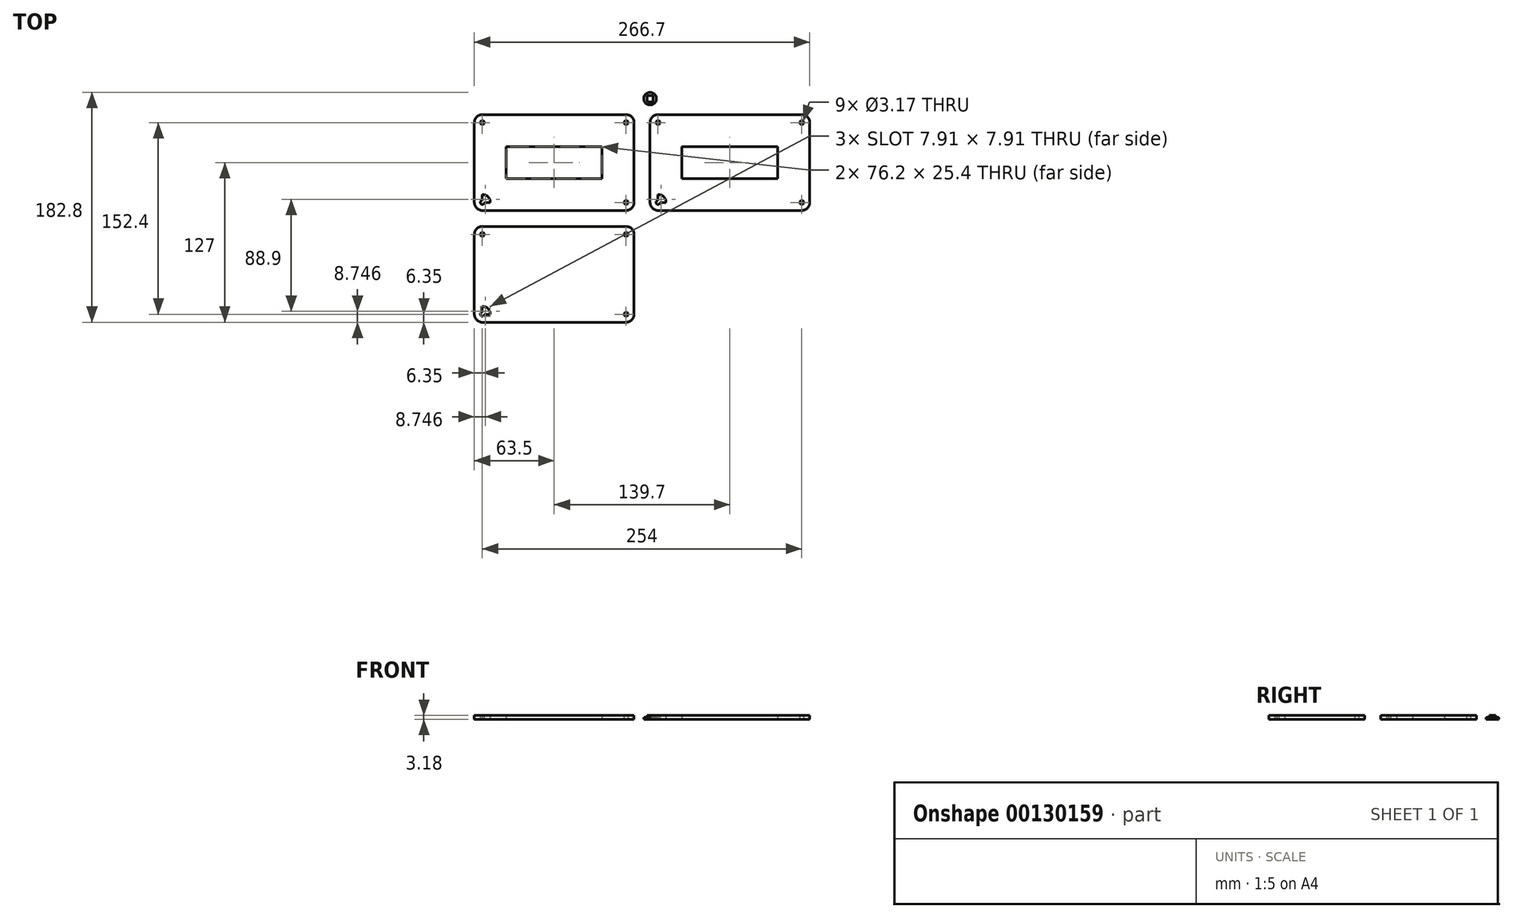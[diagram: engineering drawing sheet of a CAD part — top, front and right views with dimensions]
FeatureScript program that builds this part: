
annotation { "Feature Type Name" : "Feature", "Feature Type Description" : "" }
export const myFeature = defineFeature(function(context is Context, id is Id, definition is map)
    precondition{}
    {
        {
            var Q0;
            Q0=qCreatedBy(makeId("Top.planeOp"),FACE);
            var sketch = newSketch(context, id + "F0", { "sketchPlane" : qUnion([Q0])});
            skCircle(sketch, "E0", {"center": v(0, 0) * mm, "radius": 5 * mm});
            skLineSegment(sketch, "E1.bottom", {"start": v(-2.5, 2.5) * mm, "end": v(2.5, 2.5) * mm});
            skLineSegment(sketch, "E1.top", {"start": v(-2.5, -2.5) * mm, "end": v(2.5, -2.5) * mm});
            skLineSegment(sketch, "E1.left", {"start": v(-2.5, 2.5) * mm, "end": v(-2.5, -2.5) * mm});
            skLineSegment(sketch, "E1.right", {"start": v(2.5, 2.5) * mm, "end": v(2.5, -2.5) * mm});
            skLineSegment(sketch, "E2.bottom", {"start": v(6.35, -12.7) * mm, "end": v(120.65, -12.7) * mm});
            skLineSegment(sketch, "E2.top", {"start": v(6.35, -88.9) * mm, "end": v(120.65, -88.9) * mm});
            skLineSegment(sketch, "E2.left", {"start": v(0, -19.05) * mm, "end": v(0, -82.55) * mm});
            skLineSegment(sketch, "E2.right", {"start": v(127, -19.05) * mm, "end": v(127, -82.55) * mm});
            skLineSegment(sketch, "E3.bottom", {"start": v(25.4, -38.1) * mm, "end": v(101.6, -38.1) * mm});
            skLineSegment(sketch, "E3.top", {"start": v(25.4, -63.5) * mm, "end": v(101.6, -63.5) * mm});
            skLineSegment(sketch, "E3.left", {"start": v(25.4, -38.1) * mm, "end": v(25.4, -63.5) * mm});
            skLineSegment(sketch, "E3.right", {"start": v(101.6, -38.1) * mm, "end": v(101.6, -63.5) * mm});
            skPoint(sketch, "E4.visualSharp", {"position": v(0, -12.7) * mm});
            skArc(sketch, "E4.filletArc", {"start": v(6.35, -12.7) * mm, "mid": v(1.86, -14.56) * mm, "end": v(0, -19.05) * mm});
            skPoint(sketch, "E5.visualSharp", {"position": v(127, -12.7) * mm});
            skArc(sketch, "E5.filletArc", {"start": v(127, -19.05) * mm, "mid": v(125.14, -14.56) * mm, "end": v(120.65, -12.7) * mm});
            skPoint(sketch, "E6.visualSharp", {"position": v(127, -88.9) * mm});
            skArc(sketch, "E6.filletArc", {"start": v(120.65, -88.9) * mm, "mid": v(125.14, -87.04) * mm, "end": v(127, -82.55) * mm});
            skPoint(sketch, "E7.visualSharp", {"position": v(0, -88.9) * mm});
            skArc(sketch, "E7.filletArc", {"start": v(0, -82.55) * mm, "mid": v(1.86, -87.04) * mm, "end": v(6.35, -88.9) * mm});
            skCircle(sketch, "E8", {"center": v(6.35, -19.05) * mm, "radius": 1.59 * mm});
            skCircle(sketch, "E9", {"center": v(120.65, -19.05) * mm, "radius": 1.59 * mm});
            skCircle(sketch, "E10", {"center": v(120.65, -82.55) * mm, "radius": 1.59 * mm});
            skCircle(sketch, "E11", {"center": v(6.35, -82.55) * mm, "radius": 1.59 * mm});
            skLineSegment(sketch, "E12.bottom", {"start": v(6.35, -19.05) * mm, "end": v(120.65, -19.05) * mm});
            skLineSegment(sketch, "E12.top", {"start": v(6.35, -82.55) * mm, "end": v(120.65, -82.55) * mm});
            skLineSegment(sketch, "E12.left", {"start": v(6.35, -19.05) * mm, "end": v(6.35, -82.55) * mm});
            skLineSegment(sketch, "E12.right", {"start": v(120.65, -19.05) * mm, "end": v(120.65, -82.55) * mm});
            skArc(sketch, "E13", {"start": v(6.35, -25.4) * mm, "mid": v(10.84, -23.54) * mm, "end": v(12.7, -19.05) * mm});
            skArc(sketch, "E14", {"start": v(114.3, -19.05) * mm, "mid": v(116.16, -23.54) * mm, "end": v(120.65, -25.4) * mm});
            skArc(sketch, "E15", {"start": v(120.65, -76.2) * mm, "mid": v(116.16, -78.06) * mm, "end": v(114.3, -82.55) * mm});
            skArc(sketch, "E16", {"start": v(6.35, -76.2) * mm, "mid": v(10.84, -78.06) * mm, "end": v(12.7, -82.55) * mm});
            skSolve(sketch);
        }
        {
            var Q0;
            Q0=makeQuery(id+"F0.imprint","IMPRINT",FACE,{"disambiguationData":[TD([[makeQuery(id+"F0.imprint","IMPRINT",EDGE,{"derivedFrom":sQuery(id+"F0.wireOp",EDGE,"E1.bottom")}),-1.0]])]});
            var Q1;
            Q1=makeQuery(id+"F0.imprint","IMPRINT",FACE,{"disambiguationData":[TD([[makeQuery(id+"F0.imprint","IMPRINT",EDGE,{"derivedFrom":sQuery(id+"F0.wireOp",EDGE,"E0")}),1.0]])]});
            extrude(context, id + "F1", {"entities" : qUnion([Q0, Q1]), "depth" : 1.5 * mm});
        }
        {
            var Q0;
            Q0=makeQuery(id+"F0.imprint","IMPRINT",FACE,{"disambiguationData":[TD([[makeQuery(id+"F0.imprint","IMPRINT",EDGE,{"derivedFrom":sQuery(id+"F0.wireOp",EDGE,"E1.bottom")}),-1.0]])]});
            extrude(context, id + "F2", {"entities" : qUnion([Q0]), "operationType" : NewBodyOperationType.ADD, "depth" : 3 * mm});
        }
        {
            var Q0;
            Q0=makeQuery(id+"F0.imprint","IMPRINT",FACE,{"disambiguationData":[TD([[makeQuery(id+"F0.imprint","IMPRINT",EDGE,{"derivedFrom":sQuery(id+"F0.wireOp",EDGE,"E2.bottom")}),-1.0]])]});
            var Q1;
            {var subQ5=sQuery(id+"F0.wireOp",EDGE,"E13");Q1=makeQuery(id+"F0.imprint","IMPRINT",FACE,{"disambiguationData":[TD([[makeQuery(id+"F0.imprint","IMPRINT",EDGE,{"derivedFrom":subQ5}),1.0]])]});}
            var Q2;
            {var subQ5=sQuery(id+"F0.wireOp",EDGE,"E16");Q2=makeQuery(id+"F0.imprint","IMPRINT",FACE,{"disambiguationData":[TD([[makeQuery(id+"F0.imprint","IMPRINT",EDGE,{"derivedFrom":subQ5}),-1.0]])]});}
            var Q3;
            {var subQ5=sQuery(id+"F0.wireOp",EDGE,"E15");Q3=makeQuery(id+"F0.imprint","IMPRINT",FACE,{"disambiguationData":[TD([[makeQuery(id+"F0.imprint","IMPRINT",EDGE,{"derivedFrom":subQ5}),1.0]])]});}
            var Q4;
            {var subQ5=sQuery(id+"F0.wireOp",EDGE,"E14");Q4=makeQuery(id+"F0.imprint","IMPRINT",FACE,{"disambiguationData":[TD([[makeQuery(id+"F0.imprint","IMPRINT",EDGE,{"derivedFrom":subQ5}),1.0]])]});}
            var Q5;
            Q5=makeQuery(id+"F0.imprint","IMPRINT",FACE,{"disambiguationData":[TD([[makeQuery(id+"F0.imprint","IMPRINT",EDGE,{"derivedFrom":sQuery(id+"F0.wireOp",EDGE,"E3.bottom")}),1.0]])]});
            extrude(context, id + "F3", {"entities" : qUnion([Q0, Q1, Q2, Q3, Q4, Q5]), "depth" : 3.17 * mm});
        }
        {
            var Q0;
            Q0=makeQuery(id+"F3.opExtrude","SWEPT_BODY",BODY,{"disambiguationData":[OSD([sQuery(id+"F0.wireOp",EDGE,"E2.bottom"),sQuery(id+"F0.wireOp",EDGE,"E2.top"),sQuery(id+"F0.wireOp",EDGE,"E2.left"),sQuery(id+"F0.wireOp",EDGE,"E2.right"),sQuery(id+"F0.wireOp",EDGE,"E3.bottom"),sQuery(id+"F0.wireOp",EDGE,"E3.top"),sQuery(id+"F0.wireOp",EDGE,"E3.left"),sQuery(id+"F0.wireOp",EDGE,"E3.right"),sQuery(id+"F0.wireOp",EDGE,"E4.filletArc"),sQuery(id+"F0.wireOp",EDGE,"E5.filletArc"),sQuery(id+"F0.wireOp",EDGE,"E6.filletArc"),sQuery(id+"F0.wireOp",EDGE,"E7.filletArc")])]});
            transform(context, id + "F4", {"entities" : qUnion([Q0]), "transformType" : TransformType.TRANSLATION_3D, "dx" : -139.7 * mm, "dy" : 0 * mm, "dz" : 0 * mm, "makeCopy" : false});
        }
        {
            var Q0;
            Q0=makeQuery(id+"F0.imprint","IMPRINT",FACE,{"disambiguationData":[TD([[makeQuery(id+"F0.imprint","IMPRINT",EDGE,{"derivedFrom":sQuery(id+"F0.wireOp",EDGE,"E3.bottom")}),-1.0]])]});
            var Q1;
            Q1=makeQuery(id+"F0.imprint","IMPRINT",FACE,{"disambiguationData":[TD([[makeQuery(id+"F0.imprint","IMPRINT",EDGE,{"derivedFrom":sQuery(id+"F0.wireOp",EDGE,"E2.bottom")}),-1.0]])]});
            var Q2;
            Q2=makeQuery(id+"F0.imprint","IMPRINT",FACE,{"disambiguationData":[TD([[makeQuery(id+"F0.imprint","IMPRINT",EDGE,{"derivedFrom":sQuery(id+"F0.wireOp",EDGE,"E3.bottom")}),1.0]])]});
            var Q3;
            {var subQ5=sQuery(id+"F0.wireOp",EDGE,"E14");Q3=makeQuery(id+"F0.imprint","IMPRINT",FACE,{"disambiguationData":[TD([[makeQuery(id+"F0.imprint","IMPRINT",EDGE,{"derivedFrom":subQ5}),1.0]])]});}
            var Q4;
            {var subQ5=sQuery(id+"F0.wireOp",EDGE,"E13");Q4=makeQuery(id+"F0.imprint","IMPRINT",FACE,{"disambiguationData":[TD([[makeQuery(id+"F0.imprint","IMPRINT",EDGE,{"derivedFrom":subQ5}),1.0]])]});}
            var Q5;
            {var subQ5=sQuery(id+"F0.wireOp",EDGE,"E16");Q5=makeQuery(id+"F0.imprint","IMPRINT",FACE,{"disambiguationData":[TD([[makeQuery(id+"F0.imprint","IMPRINT",EDGE,{"derivedFrom":subQ5}),-1.0]])]});}
            var Q6;
            {var subQ5=sQuery(id+"F0.wireOp",EDGE,"E15");Q6=makeQuery(id+"F0.imprint","IMPRINT",FACE,{"disambiguationData":[TD([[makeQuery(id+"F0.imprint","IMPRINT",EDGE,{"derivedFrom":subQ5}),1.0]])]});}
            extrude(context, id + "F5", {"entities" : qUnion([Q0, Q1, Q2, Q3, Q4, Q5, Q6]), "depth" : 3.17 * mm});
        }
        {
            var Q0;
            Q0=makeQuery(id+"F5.opExtrude","SWEPT_BODY",BODY,{"disambiguationData":[OSD([sQuery(id+"F0.wireOp",EDGE,"E2.bottom"),sQuery(id+"F0.wireOp",EDGE,"E2.top"),sQuery(id+"F0.wireOp",EDGE,"E2.left"),sQuery(id+"F0.wireOp",EDGE,"E2.right"),sQuery(id+"F0.wireOp",EDGE,"E4.filletArc"),sQuery(id+"F0.wireOp",EDGE,"E5.filletArc"),sQuery(id+"F0.wireOp",EDGE,"E6.filletArc"),sQuery(id+"F0.wireOp",EDGE,"E7.filletArc"),sQuery(id+"F0.wireOp",EDGE,"E8"),sQuery(id+"F0.wireOp",EDGE,"E9"),sQuery(id+"F0.wireOp",EDGE,"E10"),sQuery(id+"F0.wireOp",EDGE,"E11")])]});
            transform(context, id + "F6", {"entities" : qUnion([Q0]), "transformType" : TransformType.TRANSLATION_3D, "dx" : -139.7 * mm, "dy" : -88.9 * mm, "dz" : 0 * mm, "makeCopy" : false});
        }
        {
            var Q0;
            Q0=makeQuery(id+"F0.imprint","IMPRINT",FACE,{"disambiguationData":[TD([[makeQuery(id+"F0.imprint","IMPRINT",EDGE,{"derivedFrom":sQuery(id+"F0.wireOp",EDGE,"E2.bottom")}),-1.0]])]});
            var Q1;
            {var subQ5=sQuery(id+"F0.wireOp",EDGE,"E13");Q1=makeQuery(id+"F0.imprint","IMPRINT",FACE,{"disambiguationData":[TD([[makeQuery(id+"F0.imprint","IMPRINT",EDGE,{"derivedFrom":subQ5}),1.0]])]});}
            var Q2;
            {var subQ5=sQuery(id+"F0.wireOp",EDGE,"E14");Q2=makeQuery(id+"F0.imprint","IMPRINT",FACE,{"disambiguationData":[TD([[makeQuery(id+"F0.imprint","IMPRINT",EDGE,{"derivedFrom":subQ5}),1.0]])]});}
            var Q3;
            {var subQ5=sQuery(id+"F0.wireOp",EDGE,"E16");Q3=makeQuery(id+"F0.imprint","IMPRINT",FACE,{"disambiguationData":[TD([[makeQuery(id+"F0.imprint","IMPRINT",EDGE,{"derivedFrom":subQ5}),-1.0]])]});}
            var Q4;
            {var subQ5=sQuery(id+"F0.wireOp",EDGE,"E15");Q4=makeQuery(id+"F0.imprint","IMPRINT",FACE,{"disambiguationData":[TD([[makeQuery(id+"F0.imprint","IMPRINT",EDGE,{"derivedFrom":subQ5}),1.0]])]});}
            extrude(context, id + "F7", {"entities" : qUnion([Q0, Q1, Q2, Q3, Q4]), "depth" : 3.17 * mm});
        }
    });
